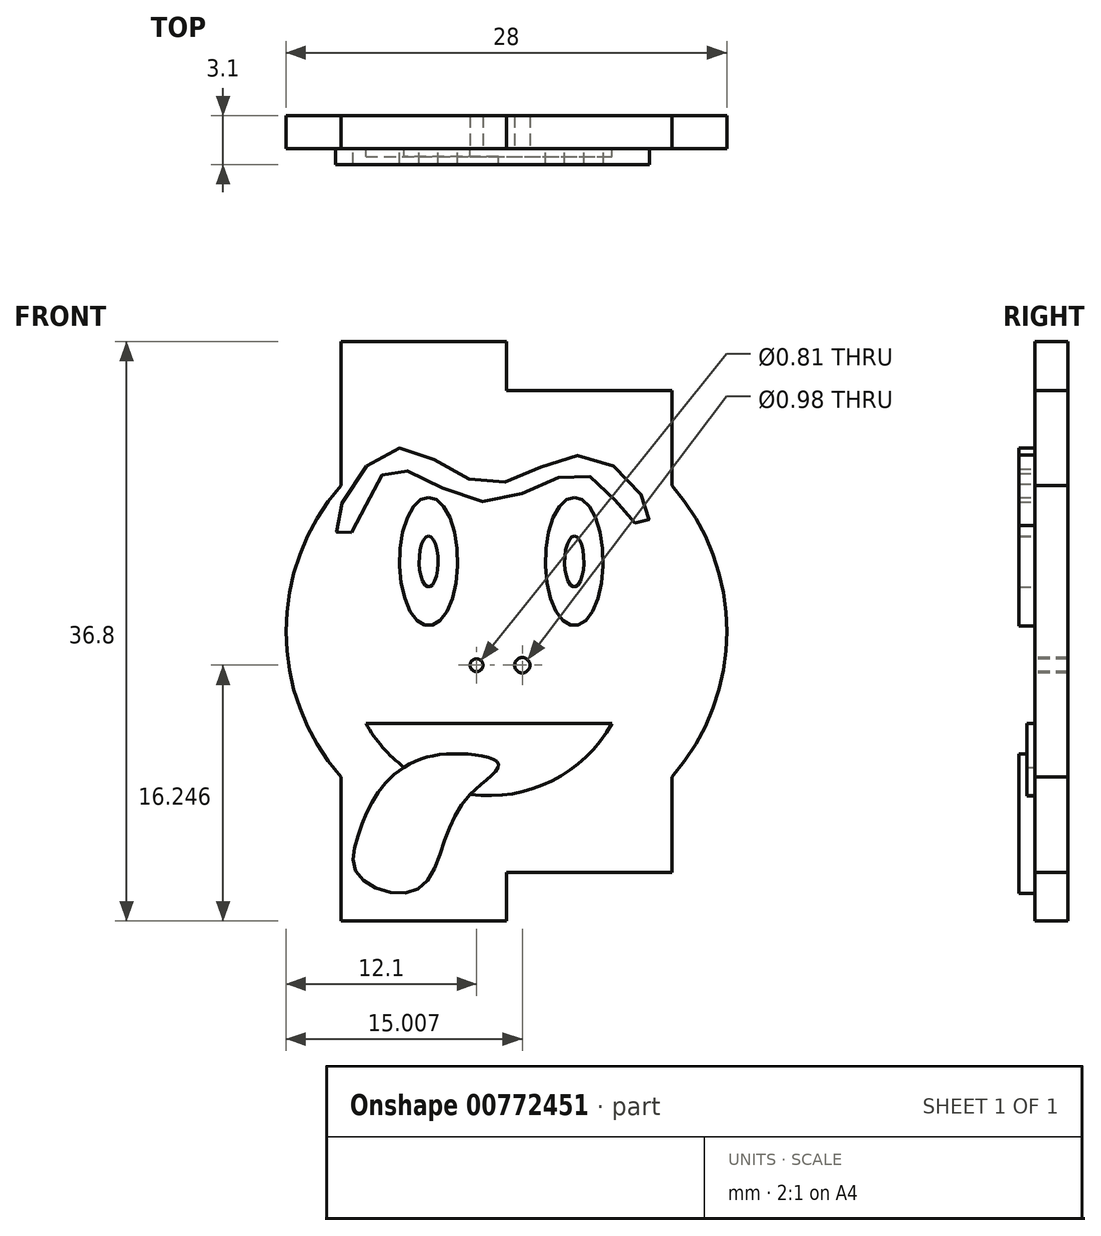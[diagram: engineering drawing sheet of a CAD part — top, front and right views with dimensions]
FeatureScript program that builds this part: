
annotation { "Feature Type Name" : "Feature", "Feature Type Description" : "" }
export const myFeature = defineFeature(function(context is Context, id is Id, definition is map)
    precondition{}
    {
        {
            var Q0;
            Q0=qCreatedBy(makeId("Front.planeOp"),FACE);
            var sketch = newSketch(context, id + "F0", { "sketchPlane" : qUnion([Q0])});
            skArc(sketch, "E0", {"start": v(-10.5, 9.26) * mm, "mid": v(-14, 0) * mm, "end": v(-10.5, -9.26) * mm});
            skLineSegment(sketch, "E1", {"start": v(-10.5, -9.26) * mm, "end": v(-10.5, -18.4) * mm});
            skLineSegment(sketch, "E2", {"start": v(-10.5, -18.4) * mm, "end": v(0, -18.4) * mm});
            skLineSegment(sketch, "E3", {"start": v(0, -18.4) * mm, "end": v(0, -15.3) * mm});
            skLineSegment(sketch, "E4", {"start": v(0, -15.3) * mm, "end": v(10.5, -15.3) * mm});
            skLineSegment(sketch, "E5", {"start": v(10.5, -15.3) * mm, "end": v(10.5, -9.26) * mm});
            skLineSegment(sketch, "E6", {"start": v(-10.5, 9.26) * mm, "end": v(-10.5, 18.4) * mm});
            skLineSegment(sketch, "E7", {"start": v(-10.5, 18.4) * mm, "end": v(0, 18.4) * mm});
            skLineSegment(sketch, "E8", {"start": v(0, 18.4) * mm, "end": v(0, 15.3) * mm});
            skLineSegment(sketch, "E9", {"start": v(0, 15.3) * mm, "end": v(10.5, 15.3) * mm});
            skLineSegment(sketch, "E10", {"start": v(10.5, 15.3) * mm, "end": v(10.5, 9.26) * mm});
            skArc(sketch, "E11.trimOffspring", {"start": v(10.5, -9.26) * mm, "mid": v(14, 0) * mm, "end": v(10.5, 9.26) * mm});
            skSolve(sketch);
        }
        {
            var Q0;
            Q0=makeQuery(id+"F0.imprint","IMPRINT",FACE,{"disambiguationData":[TD([[makeQuery(id+"F0.imprint","IMPRINT",EDGE,{"derivedFrom":sQuery(id+"F0.wireOp",EDGE,"E0")}),1.0]])]});
            extrude(context, id + "F1", {"entities" : qUnion([Q0]), "depth" : 2.1 * mm, "offsetDistance" : 25 * mm});
        }
        {
            var Q0;
            Q0=makeQuery(id+"F1.opExtrude","CAP_FACE",FACE,{"disambiguationData":[OSD([sQuery(id+"F0.wireOp",EDGE,"E0"),sQuery(id+"F0.wireOp",EDGE,"E1"),sQuery(id+"F0.wireOp",EDGE,"E2"),sQuery(id+"F0.wireOp",EDGE,"E3"),sQuery(id+"F0.wireOp",EDGE,"E4"),sQuery(id+"F0.wireOp",EDGE,"E5"),sQuery(id+"F0.wireOp",EDGE,"E6"),sQuery(id+"F0.wireOp",EDGE,"E7"),sQuery(id+"F0.wireOp",EDGE,"E8"),sQuery(id+"F0.wireOp",EDGE,"E9"),sQuery(id+"F0.wireOp",EDGE,"E10"),sQuery(id+"F0.wireOp",EDGE,"E11.trimOffspring")])],"isStart":false});
            var sketch = newSketch(context, id + "F2", { "sketchPlane" : qUnion([Q0])});
            skEllipse(sketch, "E12", {"center": v(-4.94, 4.43) * mm, "majorRadius": 4.08 * mm, "minorRadius": 1.85 * mm, "majorAxis": v(0, 1)});
            skEllipse(sketch, "E13", {"center": v(4.3, 4.43) * mm, "majorRadius": 4.08 * mm, "minorRadius": 1.84 * mm, "majorAxis": v(0, 1)});
            skPoint(sketch, "E13.centerSnap0", {"position": v(-3.1, 4.43) * mm});
            skEllipse(sketch, "E14", {"center": v(-4.94, 4.43) * mm, "majorRadius": 1.6 * mm, "minorRadius": 0.6 * mm, "majorAxis": v(0, 1)});
            skEllipse(sketch, "E15", {"center": v(4.3, 4.43) * mm, "majorRadius": 1.6 * mm, "minorRadius": 0.61 * mm, "majorAxis": v(0, 1)});
            skFitSpline(sketch, "E16", {"points": [v(-9.83, 6.27) * mm, v(-7.47, 10.23) * mm, v(-1.38, 8.22) * mm, v(5, 9.95) * mm, v(8.33, 6.79) * mm, v(9.08, 7.3) * mm, v(5.23, 11.15) * mm, v(-1.2, 9.37) * mm, v(-7.3, 11.56) * mm, v(-10.8, 6.38) * mm, v(-9.83, 6.27) * mm]});
            skArc(sketch, "E17", {"start": v(-8.93, -5.85) * mm, "mid": v(-1.11, -10.44) * mm, "end": v(6.7, -5.85) * mm});
            skLineSegment(sketch, "E18", {"start": v(-8.93, -5.85) * mm, "end": v(6.7, -5.85) * mm});
            skFitSpline(sketch, "E19", {"points": [v(-2.75, -7.79) * mm, v(-5.96, -8.33) * mm, v(-8.14, -10.2) * mm, v(-9.35, -12.75) * mm, v(-9.47, -15.42) * mm, v(-5.9, -16.5) * mm, v(-3.96, -13.42) * mm, v(-2.3, -10.36) * mm, v(-0.5, -8.45) * mm, v(-2.75, -7.79) * mm]});
            skPoint(sketch, "E20.centerSnap0", {"position": v(-4.34, 4.43) * mm});
            skPoint(sketch, "E20.center.orphan", {"position": v(-4.34, -1.67) * mm});
            skCircle(sketch, "E21", {"center": v(-1.9, -2.15) * mm, "radius": 0.4 * mm});
            skCircle(sketch, "E22", {"center": v(1, -2.15) * mm, "radius": 0.49 * mm});
            skSolve(sketch);
        }
        {
            var Q0;
            Q0=makeQuery(id+"F2.imprint","IMPRINT",FACE,{"disambiguationData":[TD([[makeQuery(id+"F2.imprint","IMPRINT",EDGE,{"derivedFrom":sQuery(id+"F2.wireOp",EDGE,"E22")}),1.0]])]});
            var Q1;
            Q1=makeQuery(id+"F2.imprint","IMPRINT",FACE,{"disambiguationData":[TD([[makeQuery(id+"F2.imprint","IMPRINT",EDGE,{"derivedFrom":sQuery(id+"F2.wireOp",EDGE,"E21")}),1.0]])]});
            extrude(context, id + "F3", {"entities" : qUnion([Q0, Q1]), "operationType" : NewBodyOperationType.REMOVE, "oppositeDirection" : true, "depth" : 25 * mm, "offsetDistance" : 25 * mm});
        }
        {
            var Q0;
            Q0=makeQuery(id+"F2.imprint","IMPRINT",FACE,{"disambiguationData":[TD([[makeQuery(id+"F2.imprint","IMPRINT",EDGE,{"derivedFrom":sQuery(id+"F2.wireOp",EDGE,"E16")}),1.0]])]});
            var Q1;
            Q1=makeQuery(id+"F2.imprint","IMPRINT",FACE,{"disambiguationData":[TD([[makeQuery(id+"F2.imprint","IMPRINT",EDGE,{"derivedFrom":sQuery(id+"F2.wireOp",EDGE,"E12")}),1.0]])]});
            var Q2;
            Q2=makeQuery(id+"F2.imprint","IMPRINT",FACE,{"disambiguationData":[TD([[makeQuery(id+"F2.imprint","IMPRINT",EDGE,{"derivedFrom":sQuery(id+"F2.wireOp",EDGE,"E13")}),1.0]])]});
            var Q3;
            {var subQ0=sQuery(id+"F2.wireOp",EDGE,"E19");var subQ1=sQuery(id+"F2.wireOp",EDGE,"E17");var subQ2=makeQuery(id+"F2.imprint","INTERSECT",VERTEX,{"disambiguationData":[OD(0.0)],"derivedFrom":[subQ1,subQ0]});Q3=makeQuery(id+"F2.imprint","IMPRINT",FACE,{"disambiguationData":[TD([[makeQuery(id+"F2.imprint","IMPRINT",EDGE,{"disambiguationData":[TD([[subQ2,-1.0]])],"derivedFrom":subQ1}),-1.0]])]});}
            var Q4;
            {var subQ0=sQuery(id+"F2.wireOp",EDGE,"E19");var subQ1=sQuery(id+"F2.wireOp",EDGE,"E17");var subQ2=makeQuery(id+"F2.imprint","INTERSECT",VERTEX,{"disambiguationData":[OD(0.0)],"derivedFrom":[subQ1,subQ0]});Q4=makeQuery(id+"F2.imprint","IMPRINT",FACE,{"disambiguationData":[TD([[makeQuery(id+"F2.imprint","IMPRINT",EDGE,{"disambiguationData":[TD([[subQ2,-1.0]])],"derivedFrom":subQ1}),1.0]])]});}
            extrude(context, id + "F4", {"entities" : qUnion([Q0, Q1, Q2, Q3, Q4]), "operationType" : NewBodyOperationType.ADD, "depth" : 1 * mm, "offsetDistance" : 25 * mm});
        }
        {
            var Q0;
            {var subQ0=sQuery(id+"F2.wireOp",EDGE,"E18");Q0=makeQuery(id+"F2.imprint","IMPRINT",FACE,{"disambiguationData":[TD([[makeQuery(id+"F2.imprint","IMPRINT",EDGE,{"derivedFrom":subQ0}),-1.0]])]});}
            extrude(context, id + "F5", {"entities" : qUnion([Q0]), "operationType" : NewBodyOperationType.ADD, "depth" : 0.5 * mm, "offsetDistance" : 25 * mm});
        }
    });
